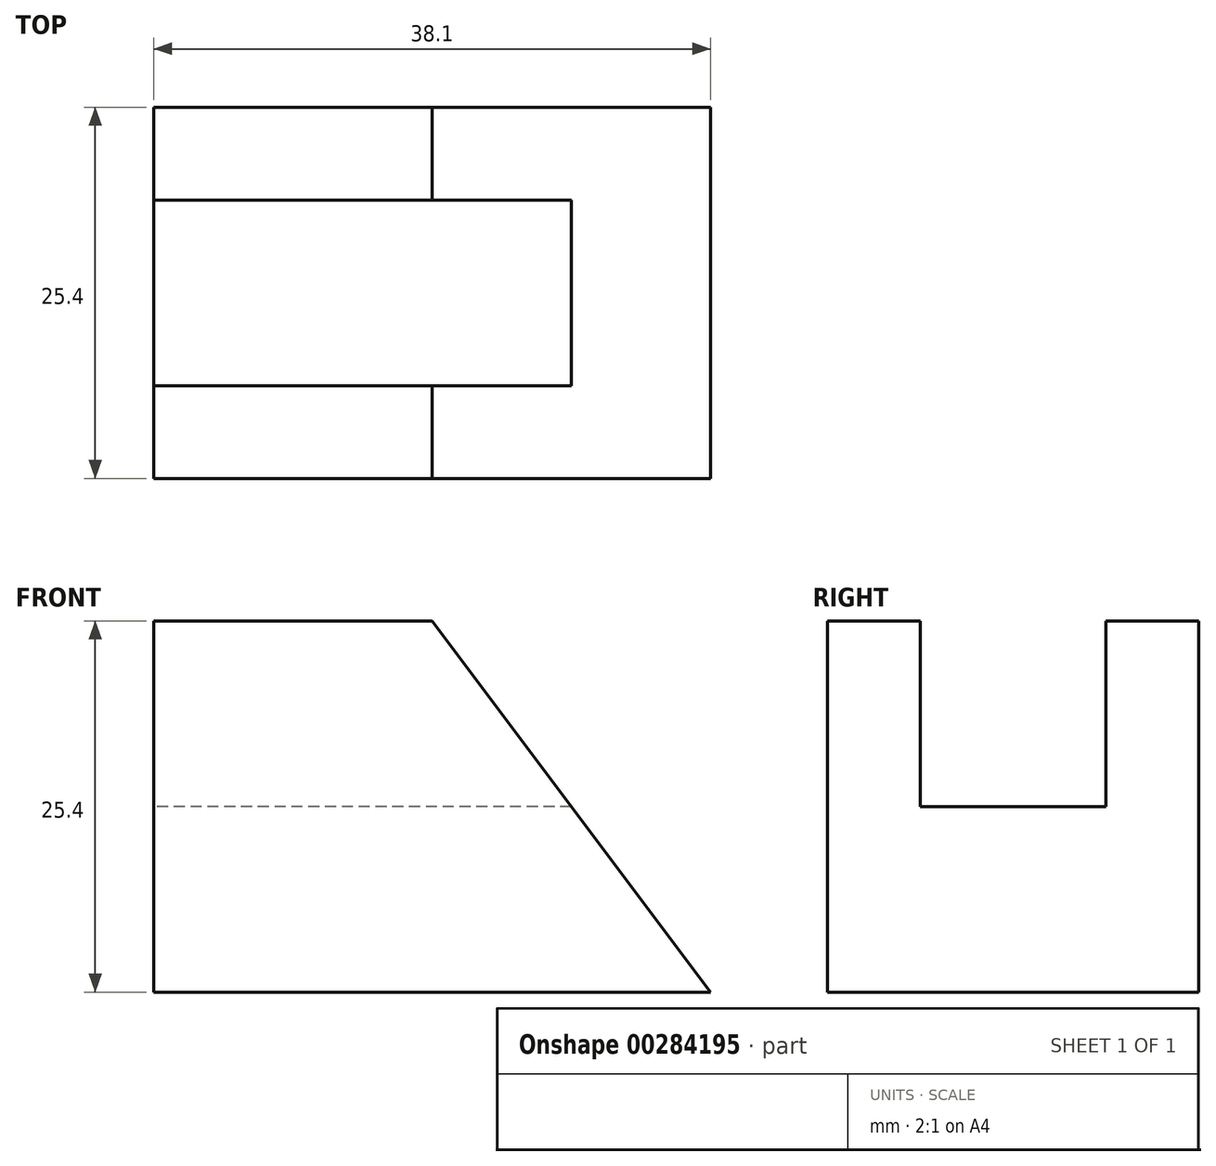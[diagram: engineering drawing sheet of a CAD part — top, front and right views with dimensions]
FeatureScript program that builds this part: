
annotation { "Feature Type Name" : "Feature", "Feature Type Description" : "" }
export const myFeature = defineFeature(function(context is Context, id is Id, definition is map)
    precondition{}
    {
        {
            var Q0;
            Q0=qCreatedBy(makeId("Front.planeOp"),FACE);
            var sketch = newSketch(context, id + "F0", { "sketchPlane" : qUnion([Q0])});
            skLineSegment(sketch, "E0", {"start": v(0, 0) * mm, "end": v(0, 25.4) * mm});
            skLineSegment(sketch, "E1", {"start": v(0, 25.4) * mm, "end": v(19.05, 25.4) * mm});
            skLineSegment(sketch, "E2", {"start": v(19.05, 25.4) * mm, "end": v(38.1, 0) * mm});
            skLineSegment(sketch, "E3", {"start": v(38.1, 0) * mm, "end": v(0, 0) * mm});
            skLineSegment(sketch, "E4", {"start": v(38.1, 0) * mm, "end": v(38.1, 25.4) * mm});
            skLineSegment(sketch, "E5", {"start": v(38.1, 25.4) * mm, "end": v(19.05, 25.4) * mm});
            skSolve(sketch);
        }
        {
            var Q0;
            Q0=qCreatedBy(makeId("Top.planeOp"),FACE);
            var sketch = newSketch(context, id + "F1", { "sketchPlane" : qUnion([Q0])});
            skLineSegment(sketch, "E6", {"start": v(0, 0) * mm, "end": v(0, 25.4) * mm});
            skLineSegment(sketch, "E7", {"start": v(0, 25.4) * mm, "end": v(38.1, 25.4) * mm});
            skLineSegment(sketch, "E8", {"start": v(38.1, 25.4) * mm, "end": v(38.1, 0) * mm});
            skLineSegment(sketch, "E9", {"start": v(0, 25.4) * mm, "end": v(0, 19.05) * mm});
            skLineSegment(sketch, "E10", {"start": v(0, 19.05) * mm, "end": v(31.75, 19.05) * mm});
            skLineSegment(sketch, "E11", {"start": v(31.75, 19.05) * mm, "end": v(31.75, 6.35) * mm});
            skLineSegment(sketch, "E12", {"start": v(31.75, 6.35) * mm, "end": v(0, 6.35) * mm});
            skLineSegment(sketch, "E13", {"start": v(0, 6.35) * mm, "end": v(0, 0) * mm});
            skLineSegment(sketch, "E14", {"start": v(18.77, 0) * mm, "end": v(18.77, 6.35) * mm});
            skLineSegment(sketch, "E15", {"start": v(18.77, 19.05) * mm, "end": v(18.77, 25.4) * mm});
            skLineSegment(sketch, "E16", {"start": v(0, 0) * mm, "end": v(38.1, 0) * mm});
            skSolve(sketch);
        }
        {
            var Q0;
            Q0 = qSketchRegion(id + "F1", true);
            extrude(context, id + "F2", {"entities" : qUnion([Q0]), "depth" : 25.4 * mm});
        }
        {
            var Q0;
            Q0=makeQuery(id+"F0.imprint","IMPRINT",FACE,{"disambiguationData":[TD([[makeQuery(id+"F0.imprint","IMPRINT",EDGE,{"derivedFrom":sQuery(id+"F0.wireOp",EDGE,"E2")}),1.0]])]});
            extrude(context, id + "F3", {"entities" : qUnion([Q0]), "operationType" : NewBodyOperationType.REMOVE, "oppositeDirection" : true, "depth" : 25.4 * mm});
        }
        {
            var Q0;
            Q0=qCreatedBy(makeId("Right.planeOp"),FACE);
            var sketch = newSketch(context, id + "F4", { "sketchPlane" : qUnion([Q0])});
            skLineSegment(sketch, "E17", {"start": v(6.35, 25.4) * mm, "end": v(6.35, 12.7) * mm});
            skLineSegment(sketch, "E18", {"start": v(6.35, 12.7) * mm, "end": v(19.05, 12.7) * mm});
            skLineSegment(sketch, "E19", {"start": v(19.05, 12.7) * mm, "end": v(19.05, 25.4) * mm});
            skLineSegment(sketch, "E20", {"start": v(6.35, 25.4) * mm, "end": v(19.05, 25.4) * mm});
            skSolve(sketch);
        }
        {
            var Q0;
            Q0 = qSketchRegion(id + "F4", true);
            extrude(context, id + "F5", {"entities" : qUnion([Q0]), "operationType" : NewBodyOperationType.REMOVE, "depth" : 31.75 * mm});
        }
    });
